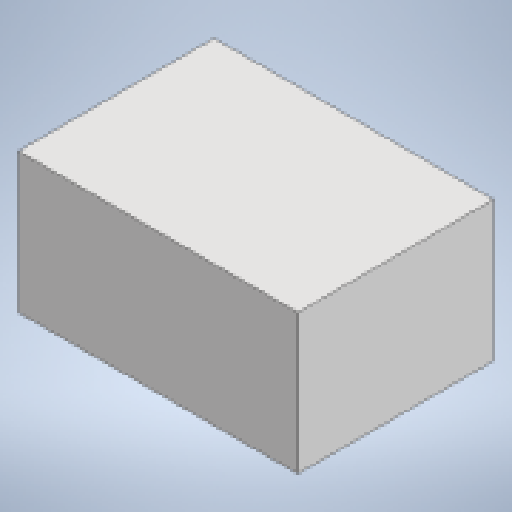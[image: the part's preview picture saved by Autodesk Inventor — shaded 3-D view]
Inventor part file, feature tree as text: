
AUTODESK INVENTOR PART (.ipt)
format: ipt  version: 2025.2 (Build 292293000, 293)  size: 105,984 bytes
history: native  units: mm
features: other x1, extrude x1, sketch x1
ambient origin geometry x8: Origin, YZ Plane, XZ Plane, XY Plane, X Axis, Y Axis, Z Axis, Center Point
bodies: Body1 (feature_tree)
feature tree (3):
  other  "ソリッド1"
  extrude  "押し出し1"  Depth=10.0mm
  sketch  "スケッチ1"
